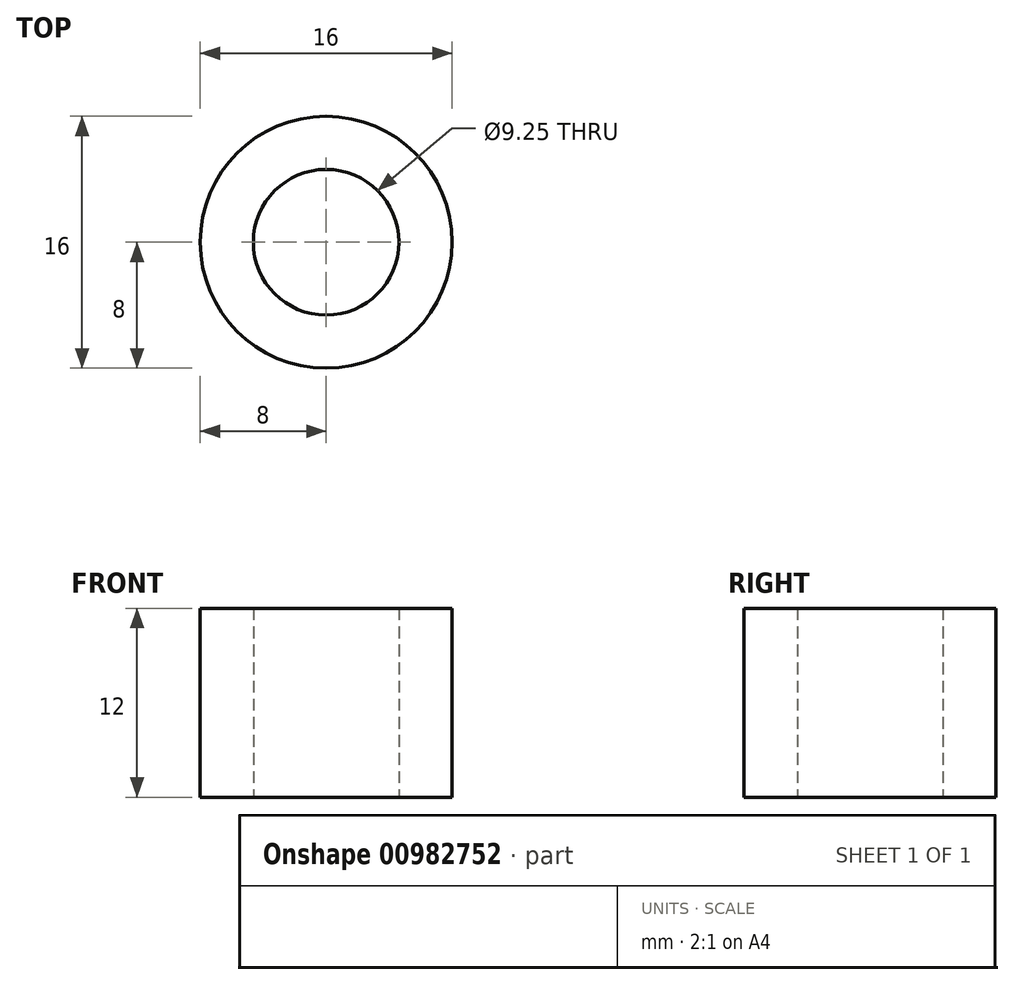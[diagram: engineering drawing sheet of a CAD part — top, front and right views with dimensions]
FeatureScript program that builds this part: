
annotation { "Feature Type Name" : "Feature", "Feature Type Description" : "" }
export const myFeature = defineFeature(function(context is Context, id is Id, definition is map)
    precondition{}
    {
        {
            var Q0;
            Q0=qCreatedBy(makeId("Top.planeOp"),FACE);
            var sketch = newSketch(context, id + "F0", { "sketchPlane" : qUnion([Q0])});
            skCircle(sketch, "E0", {"center": v(0, 0) * mm, "radius": 4.62 * mm});
            skCircle(sketch, "E1", {"center": v(0, 0) * mm, "radius": 8 * mm});
            skSolve(sketch);
        }
        {
            var Q0;
            Q0=makeQuery(id+"F0.imprint","IMPRINT",FACE,{"disambiguationData":[TD([[makeQuery(id+"F0.imprint","IMPRINT",EDGE,{"derivedFrom":sQuery(id+"F0.wireOp",EDGE,"E0")}),-1.0]])]});
            extrude(context, id + "F1", {"entities" : qUnion([Q0]), "depth" : 12 * mm, "offsetDistance" : 25 * mm});
        }
    });
